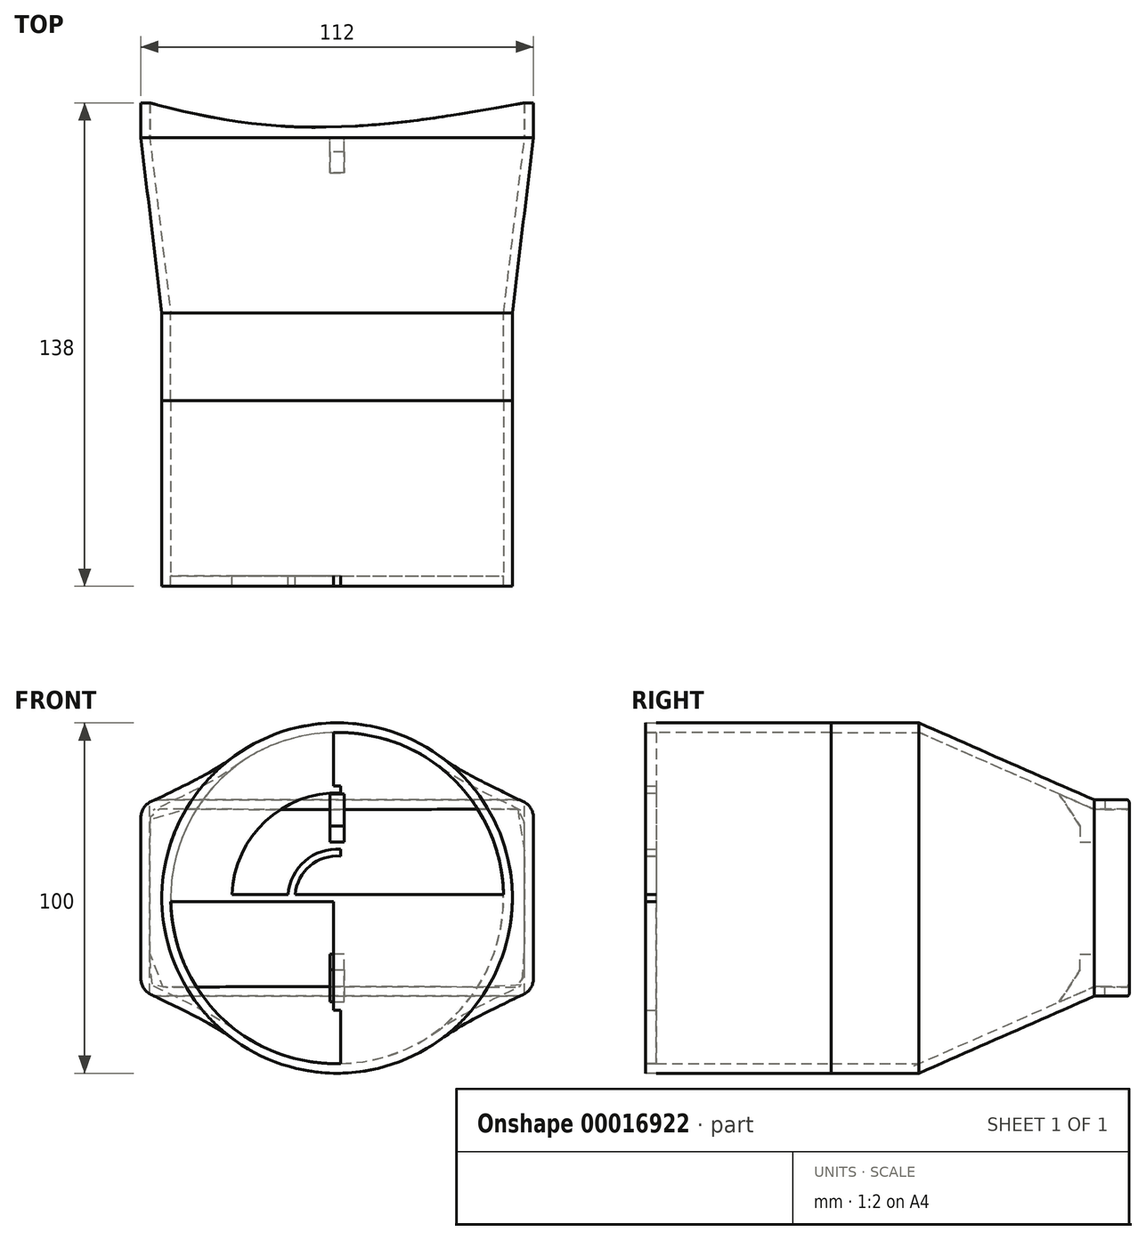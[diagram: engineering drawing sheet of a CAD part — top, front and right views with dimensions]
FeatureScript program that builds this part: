
annotation { "Feature Type Name" : "Feature", "Feature Type Description" : "" }
export const myFeature = defineFeature(function(context is Context, id is Id, definition is map)
    precondition{}
    {
        {
            var Q0;
            Q0=qCreatedBy(makeId("Front.planeOp"),FACE);
            var sketch = newSketch(context, id + "F0", { "sketchPlane" : qUnion([Q0])});
            skLineSegment(sketch, "E0.rect.bottom", {"start": v(51, 28) * mm, "end": v(-51, 28) * mm});
            skLineSegment(sketch, "E0.rect.top", {"start": v(51, -28) * mm, "end": v(-51, -28) * mm});
            skLineSegment(sketch, "E0.rect.left", {"start": v(56, 23) * mm, "end": v(56, -23) * mm});
            skLineSegment(sketch, "E0.rect.right", {"start": v(-56, 23) * mm, "end": v(-56, -23) * mm});
            skPoint(sketch, "E0.rect.middle", {"position": v(0, 0) * mm});
            skPoint(sketch, "E1.visualSharp", {"position": v(-56, 28) * mm});
            skArc(sketch, "E1.filletArc", {"start": v(-51, 28) * mm, "mid": v(-54.54, 26.54) * mm, "end": v(-56, 23) * mm});
            skPoint(sketch, "E2.visualSharp", {"position": v(-56, -28) * mm});
            skArc(sketch, "E2.filletArc", {"start": v(-56, -23) * mm, "mid": v(-54.54, -26.54) * mm, "end": v(-51, -28) * mm});
            skPoint(sketch, "E3.visualSharp", {"position": v(56, 28) * mm});
            skArc(sketch, "E3.filletArc", {"start": v(56, 23) * mm, "mid": v(54.54, 26.54) * mm, "end": v(51, 28) * mm});
            skPoint(sketch, "E4.visualSharp", {"position": v(56, -28) * mm});
            skArc(sketch, "E4.filletArc", {"start": v(51, -28) * mm, "mid": v(54.54, -26.54) * mm, "end": v(56, -23) * mm});
            skSolve(sketch);
        }
        {
            var Q0;
            Q0=qCreatedBy(makeId("Front.planeOp"),FACE);
            cPlane(context, id + "F1", {"entities" : qUnion([Q0]), "cplaneType" : CPlaneType.OFFSET, "offset" : 50 * mm, "width" : 150 * mm, "height" : 150 * mm});
        }
        {
            var Q0;
            Q0=qCreatedBy(id+"F1.planeOp",FACE);
            var sketch = newSketch(context, id + "F2", { "sketchPlane" : qUnion([Q0])});
            skPoint(sketch, "E5", {"position": v(-32.5, 38) * mm});
            skPoint(sketch, "E6", {"position": v(-39.41, 30.77) * mm});
            skPoint(sketch, "E7", {"position": v(-39.41, -30.77) * mm});
            skPoint(sketch, "E8", {"position": v(-32.5, -38) * mm});
            skPoint(sketch, "E9", {"position": v(32.5, -38) * mm});
            skPoint(sketch, "E10", {"position": v(39.41, -30.77) * mm});
            skPoint(sketch, "E11", {"position": v(39.41, 30.77) * mm});
            skPoint(sketch, "E12", {"position": v(32.5, 38) * mm});
            skArc(sketch, "E13", {"start": v(-32.63, 37.89) * mm, "mid": v(-36.24, 34.45) * mm, "end": v(-39.5, 30.66) * mm});
            skArc(sketch, "E14", {"start": v(-39.5, 30.66) * mm, "mid": v(-50, -0.08) * mm, "end": v(-39.4, -30.79) * mm});
            skArc(sketch, "E15", {"start": v(-39.4, -30.79) * mm, "mid": v(-36.12, -34.58) * mm, "end": v(-32.48, -38.02) * mm});
            skArc(sketch, "E16", {"start": v(-32.48, -38.02) * mm, "mid": v(0.03, -50) * mm, "end": v(32.52, -37.98) * mm});
            skArc(sketch, "E17", {"start": v(32.52, -37.98) * mm, "mid": v(36.14, -34.55) * mm, "end": v(39.4, -30.78) * mm});
            skArc(sketch, "E18", {"start": v(39.4, -30.78) * mm, "mid": v(50, -0.02) * mm, "end": v(39.42, 30.75) * mm});
            skArc(sketch, "E19", {"start": v(39.42, 30.75) * mm, "mid": v(36.13, 34.56) * mm, "end": v(32.48, 38.01) * mm});
            skArc(sketch, "E20", {"start": v(32.48, 38.01) * mm, "mid": v(-0.1, 50) * mm, "end": v(-32.63, 37.89) * mm});
            skSolve(sketch);
        }
        {
            var Q0;
            Q0 = qSketchRegion(id + "F0", true);
            var Q1;
            Q1 = qSketchRegion(id + "F2", true);
            loft(context, id + "F3", {"sheetProfilesArray" : [{ "sheetProfileEntities" : qUnion([Q0]) }, { "sheetProfileEntities" : qUnion([Q1]) }]});
        }
        {
            var Q0;
            Q0=makeQuery(id+"F3.opLoft","CAP_FACE",FACE,{"disambiguationData":[OSD([makeQuery(id+"F2.imprint","IMPRINT",FACE,{"disambiguationData":[TD([[makeQuery(id+"F2.imprint","IMPRINT",EDGE,{"derivedFrom":sQuery(id+"F2.wireOp",EDGE,"E13")}),1.0]])]})])],"isStart":true});
            var Q1;
            Q1=makeQuery(id+"F3.opLoft","CAP_FACE",FACE,{"disambiguationData":[OSD([makeQuery(id+"F0.imprint","IMPRINT",FACE,{"disambiguationData":[TD([[makeQuery(id+"F0.imprint","IMPRINT",EDGE,{"derivedFrom":sQuery(id+"F0.wireOp",EDGE,"E0.rect.bottom")}),1.0]])]})])],"isStart":true});
            var Q2;
            Q2=makeQuery(id+"F3.opLoft","SWEPT_BODY",BODY,{"disambiguationData":[OSD([makeQuery(id+"F0.imprint","IMPRINT",FACE,{"disambiguationData":[TD([[makeQuery(id+"F0.imprint","IMPRINT",EDGE,{"derivedFrom":sQuery(id+"F0.wireOp",EDGE,"E0.rect.bottom")}),1.0]])]}),makeQuery(id+"F2.imprint","IMPRINT",FACE,{"disambiguationData":[TD([[makeQuery(id+"F2.imprint","IMPRINT",EDGE,{"derivedFrom":sQuery(id+"F2.wireOp",EDGE,"20035c58-e152-4f65-9b51-79b2b6d4c0861")}),1.0]])]})])]});
            shell(context, id + "F4", {"entities" : qUnion([Q0, Q1]), "parts" : qUnion([Q2]), "thickness" : 2.5 * mm});
        }
        {
            var Q0;
            Q0=makeQuery(id+"F3.opLoft","CAP_FACE",FACE,{"disambiguationData":[OSD([makeQuery(id+"F2.imprint","IMPRINT",FACE,{"disambiguationData":[TD([[makeQuery(id+"F2.imprint","IMPRINT",EDGE,{"derivedFrom":sQuery(id+"F2.wireOp",EDGE,"E13")}),1.0]])]})])],"isStart":true});
            extrude(context, id + "F5", {"entities" : qUnion([Q0]), "operationType" : NewBodyOperationType.ADD, "depth" : 25 * mm});
        }
        {
            var Q0;
            Q0=makeQuery(id+"F3.opLoft","CAP_FACE",FACE,{"disambiguationData":[OSD([makeQuery(id+"F0.imprint","IMPRINT",FACE,{"disambiguationData":[TD([[makeQuery(id+"F0.imprint","IMPRINT",EDGE,{"derivedFrom":sQuery(id+"F0.wireOp",EDGE,"E0.rect.bottom")}),1.0]])]})])],"isStart":true});
            extrude(context, id + "F6", {"entities" : qUnion([Q0]), "operationType" : NewBodyOperationType.ADD, "depth" : 10 * mm});
        }
        {
            var Q0;
            Q0=makeQuery(id+"F6.opExtrude","SWEPT_FACE",FACE,{"disambiguationData":[OSD([sQuery(id+"F0.wireOp",EDGE,"E0.rect.bottom"),sQuery(id+"F0.wireOp",EDGE,"E1.filletArc"),sQuery(id+"F0.wireOp",EDGE,"E3.filletArc")])]});
            var sketch = newSketch(context, id + "F7", { "sketchPlane" : qUnion([Q0])});
            skPoint(sketch, "E21.0", {"position": v(-56, 10) * mm});
            skPoint(sketch, "E22.0", {"position": v(56, 10) * mm});
            skFitSpline(sketch, "E23", {"points": [v(-53.5, 10) * mm, v(-11.54, 3.12) * mm, v(53.5, 10) * mm], "startDerivative": vector(83.97, -22.89) * mm, "endDerivative": vector(135.93, 25.6) * mm});
            skLineSegment(sketch, "E24", {"start": v(-53.5, 10) * mm, "end": v(53.5, 10) * mm});
            skSolve(sketch);
        }
        {
            var Q0;
            Q0 = qSketchRegion(id + "F7", true);
            extrude(context, id + "F8", {"entities" : qUnion([Q0]), "operationType" : NewBodyOperationType.REMOVE, "endBound" : BoundingType.THROUGH_ALL, "oppositeDirection" : true, "depth" : 25 * mm});
        }
        {
            var Q0;
            Q0=makeQuery(id+"F5.opExtrude","CAP_FACE",FACE,{"disambiguationData":[OSD([makeQuery(id+"F2.imprint","IMPRINT",FACE,{"disambiguationData":[TD([[makeQuery(id+"F2.imprint","IMPRINT",EDGE,{"derivedFrom":sQuery(id+"F2.wireOp",EDGE,"E13")}),1.0]])]})])],"isStart":false});
            extrude(context, id + "F9", {"entities" : qUnion([Q0]), "depth" : 50 * mm});
        }
        {
            var Q0;
            Q0=makeQuery(id+"F9.opExtrude","CAP_FACE",FACE,{"disambiguationData":[OSD([makeQuery(id+"F2.imprint","IMPRINT",FACE,{"disambiguationData":[TD([[makeQuery(id+"F2.imprint","IMPRINT",EDGE,{"derivedFrom":sQuery(id+"F2.wireOp",EDGE,"E13")}),1.0]])]})])],"isStart":false});
            var sketch = newSketch(context, id + "F10", { "sketchPlane" : qUnion([Q0])});
            skCircle(sketch, "E25", {"center": v(0, 0) * mm, "radius": 50 * mm});
            skCircle(sketch, "E26", {"center": v(0, 0) * mm, "radius": 32 * mm});
            skCircle(sketch, "E27", {"center": v(0, 0) * mm, "radius": 30 * mm});
            skCircle(sketch, "E28", {"center": v(0, 0) * mm, "radius": 14 * mm});
            skCircle(sketch, "E29", {"center": v(0, 0) * mm, "radius": 12 * mm});
            skLineSegment(sketch, "E30.rect.bottom", {"start": v(1, 50) * mm, "end": v(-1, 50) * mm});
            skLineSegment(sketch, "E30.rect.top", {"start": v(1, -50) * mm, "end": v(-1, -50) * mm});
            skLineSegment(sketch, "E30.rect.left", {"start": v(1, 50) * mm, "end": v(1, -50) * mm});
            skLineSegment(sketch, "E30.rect.right", {"start": v(-1, 50) * mm, "end": v(-1, -50) * mm});
            skLineSegment(sketch, "E31.rect.bottom", {"start": v(-50, 1) * mm, "end": v(50, 1) * mm});
            skLineSegment(sketch, "E31.rect.top", {"start": v(-50, -1) * mm, "end": v(50, -1) * mm});
            skLineSegment(sketch, "E31.rect.left", {"start": v(-50, 1) * mm, "end": v(-50, -1) * mm});
            skLineSegment(sketch, "E31.rect.right", {"start": v(50, 1) * mm, "end": v(50, -1) * mm});
            skSolve(sketch);
        }
        {
            var Q0;
            {var subQ5=sQuery(id+"F10.wireOp",EDGE,"E25");var subQ7=makeQuery(id+"F10.imprint","IMPRINT",VERTEX,{"disambiguationData":[OD(0.0)],"derivedFrom":subQ5});Q0=makeQuery(id+"F10.imprint","IMPRINT",FACE,{"disambiguationData":[TD([[makeQuery(id+"F10.imprint","IMPRINT",EDGE,{"disambiguationData":[TD([[subQ7,-1.0]])],"derivedFrom":subQ5}),1.0]])]});}
            var Q1;
            {var subQ6=sQuery(id+"F10.wireOp",EDGE,"E30.rect.bottom");Q1=makeQuery(id+"F10.imprint","IMPRINT",FACE,{"disambiguationData":[TD([[makeQuery(id+"F10.imprint","IMPRINT",EDGE,{"derivedFrom":subQ6}),1.0]])]});}
            var Q2;
            {var subQ3=sQuery(id+"F10.wireOp",EDGE,"E25");var subQ8=makeQuery(id+"F10.imprint","IMPRINT",VERTEX,{"disambiguationData":[OD(6.0)],"derivedFrom":subQ3});Q2=makeQuery(id+"F10.imprint","IMPRINT",FACE,{"disambiguationData":[TD([[makeQuery(id+"F10.imprint","IMPRINT",EDGE,{"disambiguationData":[TD([[subQ8,-1.0]])],"derivedFrom":subQ3}),1.0]])]});}
            var Q3;
            {var subQ5=sQuery(id+"F10.wireOp",EDGE,"E31.rect.right");Q3=makeQuery(id+"F10.imprint","IMPRINT",FACE,{"disambiguationData":[TD([[makeQuery(id+"F10.imprint","IMPRINT",EDGE,{"derivedFrom":subQ5}),-1.0]])]});}
            var Q4;
            {var subQ5=sQuery(id+"F10.wireOp",EDGE,"E25");var subQ8=makeQuery(id+"F10.imprint","IMPRINT",VERTEX,{"disambiguationData":[OD(4.0)],"derivedFrom":subQ5});Q4=makeQuery(id+"F10.imprint","IMPRINT",FACE,{"disambiguationData":[TD([[makeQuery(id+"F10.imprint","IMPRINT",EDGE,{"disambiguationData":[TD([[subQ8,-1.0]])],"derivedFrom":subQ5}),1.0]])]});}
            var Q5;
            {var subQ6=sQuery(id+"F10.wireOp",EDGE,"E30.rect.top");Q5=makeQuery(id+"F10.imprint","IMPRINT",FACE,{"disambiguationData":[TD([[makeQuery(id+"F10.imprint","IMPRINT",EDGE,{"derivedFrom":subQ6}),-1.0]])]});}
            var Q6;
            {var subQ5=sQuery(id+"F10.wireOp",EDGE,"E25");var subQ8=makeQuery(id+"F10.imprint","IMPRINT",VERTEX,{"disambiguationData":[OD(2.0)],"derivedFrom":subQ5});Q6=makeQuery(id+"F10.imprint","IMPRINT",FACE,{"disambiguationData":[TD([[makeQuery(id+"F10.imprint","IMPRINT",EDGE,{"disambiguationData":[TD([[subQ8,-1.0]])],"derivedFrom":subQ5}),1.0]])]});}
            var Q7;
            {var subQ0=sQuery(id+"F10.wireOp",EDGE,"E31.rect.left");Q7=makeQuery(id+"F10.imprint","IMPRINT",FACE,{"disambiguationData":[TD([[makeQuery(id+"F10.imprint","IMPRINT",EDGE,{"derivedFrom":subQ0}),1.0]])]});}
            var Q8;
            {var subQ3=sQuery(id+"F10.wireOp",EDGE,"E31.rect.bottom");var subQ5=sQuery(id+"F10.wireOp",EDGE,"E26");var subQ7=makeQuery(id+"F10.imprint","INTERSECT",VERTEX,{"disambiguationData":[OD(1.0)],"derivedFrom":[subQ5,subQ3]});Q8=makeQuery(id+"F10.imprint","IMPRINT",FACE,{"disambiguationData":[TD([[makeQuery(id+"F10.imprint","IMPRINT",EDGE,{"disambiguationData":[TD([[subQ7,-1.0]])],"derivedFrom":subQ5}),-1.0]])]});}
            var Q9;
            {var subQ3=sQuery(id+"F10.wireOp",EDGE,"E26");var subQ5=sQuery(id+"F10.wireOp",EDGE,"E31.rect.bottom");var subQ7=makeQuery(id+"F10.imprint","INTERSECT",VERTEX,{"disambiguationData":[OD(1.0)],"derivedFrom":[subQ3,subQ5]});Q9=makeQuery(id+"F10.imprint","IMPRINT",FACE,{"disambiguationData":[TD([[makeQuery(id+"F10.imprint","IMPRINT",EDGE,{"disambiguationData":[TD([[subQ7,-1.0]])],"derivedFrom":subQ3}),1.0]])]});}
            var Q10;
            {var subQ3=sQuery(id+"F10.wireOp",EDGE,"E27");var subQ5=sQuery(id+"F10.wireOp",EDGE,"E31.rect.bottom");var subQ7=makeQuery(id+"F10.imprint","INTERSECT",VERTEX,{"disambiguationData":[OD(1.0)],"derivedFrom":[subQ3,subQ5]});Q10=makeQuery(id+"F10.imprint","IMPRINT",FACE,{"disambiguationData":[TD([[makeQuery(id+"F10.imprint","IMPRINT",EDGE,{"disambiguationData":[TD([[subQ7,-1.0]])],"derivedFrom":subQ3}),1.0]])]});}
            var Q11;
            {var subQ3=sQuery(id+"F10.wireOp",EDGE,"E26");var subQ5=sQuery(id+"F10.wireOp",EDGE,"E30.rect.right");var subQ7=makeQuery(id+"F10.imprint","INTERSECT",VERTEX,{"disambiguationData":[OD(0.0)],"derivedFrom":[subQ3,subQ5]});Q11=makeQuery(id+"F10.imprint","IMPRINT",FACE,{"disambiguationData":[TD([[makeQuery(id+"F10.imprint","IMPRINT",EDGE,{"disambiguationData":[TD([[subQ7,-1.0]])],"derivedFrom":subQ3}),1.0]])]});}
            var Q12;
            {var subQ0=sQuery(id+"F10.wireOp",EDGE,"E31.rect.top");var subQ3=sQuery(id+"F10.wireOp",EDGE,"E26");var subQ4=makeQuery(id+"F10.imprint","INTERSECT",VERTEX,{"disambiguationData":[OD(0.0)],"derivedFrom":[subQ3,subQ0]});Q12=makeQuery(id+"F10.imprint","IMPRINT",FACE,{"disambiguationData":[TD([[makeQuery(id+"F10.imprint","IMPRINT",EDGE,{"disambiguationData":[TD([[subQ4,-1.0]])],"derivedFrom":subQ3}),1.0]])]});}
            var Q13;
            {var subQ0=sQuery(id+"F10.wireOp",EDGE,"E31.rect.top");var subQ3=sQuery(id+"F10.wireOp",EDGE,"E28");var subQ4=makeQuery(id+"F10.imprint","INTERSECT",VERTEX,{"disambiguationData":[OD(0.0)],"derivedFrom":[subQ3,subQ0]});Q13=makeQuery(id+"F10.imprint","IMPRINT",FACE,{"disambiguationData":[TD([[makeQuery(id+"F10.imprint","IMPRINT",EDGE,{"disambiguationData":[TD([[subQ4,-1.0]])],"derivedFrom":subQ3}),1.0]])]});}
            var Q14;
            {var subQ3=sQuery(id+"F10.wireOp",EDGE,"E28");var subQ5=sQuery(id+"F10.wireOp",EDGE,"E30.rect.right");var subQ7=makeQuery(id+"F10.imprint","INTERSECT",VERTEX,{"disambiguationData":[OD(0.0)],"derivedFrom":[subQ3,subQ5]});Q14=makeQuery(id+"F10.imprint","IMPRINT",FACE,{"disambiguationData":[TD([[makeQuery(id+"F10.imprint","IMPRINT",EDGE,{"disambiguationData":[TD([[subQ7,-1.0]])],"derivedFrom":subQ3}),1.0]])]});}
            var Q15;
            {var subQ3=sQuery(id+"F10.wireOp",EDGE,"E28");var subQ5=sQuery(id+"F10.wireOp",EDGE,"E31.rect.bottom");var subQ7=makeQuery(id+"F10.imprint","INTERSECT",VERTEX,{"disambiguationData":[OD(1.0)],"derivedFrom":[subQ3,subQ5]});Q15=makeQuery(id+"F10.imprint","IMPRINT",FACE,{"disambiguationData":[TD([[makeQuery(id+"F10.imprint","IMPRINT",EDGE,{"disambiguationData":[TD([[subQ7,-1.0]])],"derivedFrom":subQ3}),1.0]])]});}
            var Q16;
            {var subQ3=sQuery(id+"F10.wireOp",EDGE,"E29");var subQ5=sQuery(id+"F10.wireOp",EDGE,"E31.rect.bottom");var subQ7=makeQuery(id+"F10.imprint","INTERSECT",VERTEX,{"disambiguationData":[OD(1.0)],"derivedFrom":[subQ3,subQ5]});Q16=makeQuery(id+"F10.imprint","IMPRINT",FACE,{"disambiguationData":[TD([[makeQuery(id+"F10.imprint","IMPRINT",EDGE,{"disambiguationData":[TD([[subQ7,-1.0]])],"derivedFrom":subQ3}),1.0]])]});}
            var Q17;
            {var subQ3=sQuery(id+"F10.wireOp",EDGE,"E30.rect.left");var subQ5=sQuery(id+"F10.wireOp",EDGE,"E29");var subQ7=makeQuery(id+"F10.imprint","INTERSECT",VERTEX,{"disambiguationData":[OD(0.0)],"derivedFrom":[subQ5,subQ3]});Q17=makeQuery(id+"F10.imprint","IMPRINT",FACE,{"disambiguationData":[TD([[makeQuery(id+"F10.imprint","IMPRINT",EDGE,{"disambiguationData":[TD([[subQ7,-1.0]])],"derivedFrom":subQ5}),1.0]])]});}
            var Q18;
            {var subQ1=sQuery(id+"F10.wireOp",EDGE,"E30.rect.right");var subQ5=sQuery(id+"F10.wireOp",EDGE,"E29");var subQ6=makeQuery(id+"F10.imprint","INTERSECT",VERTEX,{"disambiguationData":[OD(1.0)],"derivedFrom":[subQ5,subQ1]});Q18=makeQuery(id+"F10.imprint","IMPRINT",FACE,{"disambiguationData":[TD([[makeQuery(id+"F10.imprint","IMPRINT",EDGE,{"disambiguationData":[TD([[subQ6,-1.0]])],"derivedFrom":subQ5}),1.0]])]});}
            var Q19;
            {var subQ3=sQuery(id+"F10.wireOp",EDGE,"E29");var subQ5=sQuery(id+"F10.wireOp",EDGE,"E31.rect.bottom");var subQ7=makeQuery(id+"F10.imprint","INTERSECT",VERTEX,{"disambiguationData":[OD(0.0)],"derivedFrom":[subQ3,subQ5]});Q19=makeQuery(id+"F10.imprint","IMPRINT",FACE,{"disambiguationData":[TD([[makeQuery(id+"F10.imprint","IMPRINT",EDGE,{"disambiguationData":[TD([[subQ7,1.0]])],"derivedFrom":subQ3}),1.0]])]});}
            var Q20;
            {var subQ3=sQuery(id+"F10.wireOp",EDGE,"E28");var subQ5=sQuery(id+"F10.wireOp",EDGE,"E30.rect.left");var subQ7=makeQuery(id+"F10.imprint","INTERSECT",VERTEX,{"disambiguationData":[OD(1.0)],"derivedFrom":[subQ3,subQ5]});Q20=makeQuery(id+"F10.imprint","IMPRINT",FACE,{"disambiguationData":[TD([[makeQuery(id+"F10.imprint","IMPRINT",EDGE,{"disambiguationData":[TD([[subQ7,-1.0]])],"derivedFrom":subQ3}),1.0]])]});}
            var Q21;
            {var subQ0=sQuery(id+"F10.wireOp",EDGE,"E30.rect.right");var subQ3=sQuery(id+"F10.wireOp",EDGE,"E28");var subQ4=makeQuery(id+"F10.imprint","INTERSECT",VERTEX,{"disambiguationData":[OD(1.0)],"derivedFrom":[subQ3,subQ0]});Q21=makeQuery(id+"F10.imprint","IMPRINT",FACE,{"disambiguationData":[TD([[makeQuery(id+"F10.imprint","IMPRINT",EDGE,{"disambiguationData":[TD([[subQ4,-1.0]])],"derivedFrom":subQ3}),1.0]])]});}
            var Q22;
            {var subQ0=sQuery(id+"F10.wireOp",EDGE,"E30.rect.right");var subQ3=sQuery(id+"F10.wireOp",EDGE,"E27");var subQ4=makeQuery(id+"F10.imprint","INTERSECT",VERTEX,{"disambiguationData":[OD(1.0)],"derivedFrom":[subQ3,subQ0]});Q22=makeQuery(id+"F10.imprint","IMPRINT",FACE,{"disambiguationData":[TD([[makeQuery(id+"F10.imprint","IMPRINT",EDGE,{"disambiguationData":[TD([[subQ4,-1.0]])],"derivedFrom":subQ3}),1.0]])]});}
            var Q23;
            {var subQ3=sQuery(id+"F10.wireOp",EDGE,"E28");var subQ5=sQuery(id+"F10.wireOp",EDGE,"E31.rect.bottom");var subQ7=makeQuery(id+"F10.imprint","INTERSECT",VERTEX,{"disambiguationData":[OD(0.0)],"derivedFrom":[subQ3,subQ5]});Q23=makeQuery(id+"F10.imprint","IMPRINT",FACE,{"disambiguationData":[TD([[makeQuery(id+"F10.imprint","IMPRINT",EDGE,{"disambiguationData":[TD([[subQ7,1.0]])],"derivedFrom":subQ3}),1.0]])]});}
            var Q24;
            {var subQ3=sQuery(id+"F10.wireOp",EDGE,"E28");var subQ5=sQuery(id+"F10.wireOp",EDGE,"E30.rect.left");var subQ7=makeQuery(id+"F10.imprint","INTERSECT",VERTEX,{"disambiguationData":[OD(0.0)],"derivedFrom":[subQ3,subQ5]});Q24=makeQuery(id+"F10.imprint","IMPRINT",FACE,{"disambiguationData":[TD([[makeQuery(id+"F10.imprint","IMPRINT",EDGE,{"disambiguationData":[TD([[subQ7,1.0]])],"derivedFrom":subQ3}),1.0]])]});}
            var Q25;
            {var subQ3=sQuery(id+"F10.wireOp",EDGE,"E28");var subQ5=sQuery(id+"F10.wireOp",EDGE,"E30.rect.left");var subQ7=makeQuery(id+"F10.imprint","INTERSECT",VERTEX,{"disambiguationData":[OD(0.0)],"derivedFrom":[subQ3,subQ5]});Q25=makeQuery(id+"F10.imprint","IMPRINT",FACE,{"disambiguationData":[TD([[makeQuery(id+"F10.imprint","IMPRINT",EDGE,{"disambiguationData":[TD([[subQ7,-1.0]])],"derivedFrom":subQ3}),1.0]])]});}
            var Q26;
            {var subQ3=sQuery(id+"F10.wireOp",EDGE,"E27");var subQ5=sQuery(id+"F10.wireOp",EDGE,"E30.rect.left");var subQ7=makeQuery(id+"F10.imprint","INTERSECT",VERTEX,{"disambiguationData":[OD(0.0)],"derivedFrom":[subQ3,subQ5]});Q26=makeQuery(id+"F10.imprint","IMPRINT",FACE,{"disambiguationData":[TD([[makeQuery(id+"F10.imprint","IMPRINT",EDGE,{"disambiguationData":[TD([[subQ7,-1.0]])],"derivedFrom":subQ3}),1.0]])]});}
            var Q27;
            {var subQ3=sQuery(id+"F10.wireOp",EDGE,"E30.rect.left");var subQ5=sQuery(id+"F10.wireOp",EDGE,"E26");var subQ6=makeQuery(id+"F10.imprint","INTERSECT",VERTEX,{"disambiguationData":[OD(0.0)],"derivedFrom":[subQ5,subQ3]});Q27=makeQuery(id+"F10.imprint","IMPRINT",FACE,{"disambiguationData":[TD([[makeQuery(id+"F10.imprint","IMPRINT",EDGE,{"disambiguationData":[TD([[subQ6,-1.0]])],"derivedFrom":subQ5}),-1.0]])]});}
            var Q28;
            {var subQ3=sQuery(id+"F10.wireOp",EDGE,"E26");var subQ5=sQuery(id+"F10.wireOp",EDGE,"E30.rect.left");var subQ7=makeQuery(id+"F10.imprint","INTERSECT",VERTEX,{"disambiguationData":[OD(0.0)],"derivedFrom":[subQ3,subQ5]});Q28=makeQuery(id+"F10.imprint","IMPRINT",FACE,{"disambiguationData":[TD([[makeQuery(id+"F10.imprint","IMPRINT",EDGE,{"disambiguationData":[TD([[subQ7,-1.0]])],"derivedFrom":subQ3}),1.0]])]});}
            var Q29;
            {var subQ3=sQuery(id+"F10.wireOp",EDGE,"E26");var subQ5=sQuery(id+"F10.wireOp",EDGE,"E30.rect.left");var subQ7=makeQuery(id+"F10.imprint","INTERSECT",VERTEX,{"disambiguationData":[OD(0.0)],"derivedFrom":[subQ3,subQ5]});Q29=makeQuery(id+"F10.imprint","IMPRINT",FACE,{"disambiguationData":[TD([[makeQuery(id+"F10.imprint","IMPRINT",EDGE,{"disambiguationData":[TD([[subQ7,1.0]])],"derivedFrom":subQ3}),1.0]])]});}
            var Q30;
            {var subQ3=sQuery(id+"F10.wireOp",EDGE,"E31.rect.bottom");var subQ5=sQuery(id+"F10.wireOp",EDGE,"E26");var subQ7=makeQuery(id+"F10.imprint","INTERSECT",VERTEX,{"disambiguationData":[OD(0.0)],"derivedFrom":[subQ5,subQ3]});Q30=makeQuery(id+"F10.imprint","IMPRINT",FACE,{"disambiguationData":[TD([[makeQuery(id+"F10.imprint","IMPRINT",EDGE,{"disambiguationData":[TD([[subQ7,1.0]])],"derivedFrom":subQ5}),-1.0]])]});}
            var Q31;
            {var subQ3=sQuery(id+"F10.wireOp",EDGE,"E26");var subQ5=sQuery(id+"F10.wireOp",EDGE,"E30.rect.left");var subQ7=makeQuery(id+"F10.imprint","INTERSECT",VERTEX,{"disambiguationData":[OD(1.0)],"derivedFrom":[subQ3,subQ5]});Q31=makeQuery(id+"F10.imprint","IMPRINT",FACE,{"disambiguationData":[TD([[makeQuery(id+"F10.imprint","IMPRINT",EDGE,{"disambiguationData":[TD([[subQ7,-1.0]])],"derivedFrom":subQ3}),1.0]])]});}
            var Q32;
            {var subQ3=sQuery(id+"F10.wireOp",EDGE,"E26");var subQ5=sQuery(id+"F10.wireOp",EDGE,"E31.rect.bottom");var subQ7=makeQuery(id+"F10.imprint","INTERSECT",VERTEX,{"disambiguationData":[OD(0.0)],"derivedFrom":[subQ3,subQ5]});Q32=makeQuery(id+"F10.imprint","IMPRINT",FACE,{"disambiguationData":[TD([[makeQuery(id+"F10.imprint","IMPRINT",EDGE,{"disambiguationData":[TD([[subQ7,1.0]])],"derivedFrom":subQ3}),1.0]])]});}
            var Q33;
            {var subQ0=sQuery(id+"F10.wireOp",EDGE,"E31.rect.bottom");var subQ3=sQuery(id+"F10.wireOp",EDGE,"E30.rect.left");var subQ4=makeQuery(id+"F10.imprint","INTERSECT",VERTEX,{"derivedFrom":[subQ3,subQ0]});Q33=makeQuery(id+"F10.imprint","IMPRINT",FACE,{"disambiguationData":[TD([[makeQuery(id+"F10.imprint","IMPRINT",EDGE,{"disambiguationData":[TD([[subQ4,-1.0]])],"derivedFrom":subQ3}),-1.0]])]});}
            var Q34;
            {var subQ3=sQuery(id+"F10.wireOp",EDGE,"E27");var subQ5=sQuery(id+"F10.wireOp",EDGE,"E31.rect.bottom");var subQ7=makeQuery(id+"F10.imprint","INTERSECT",VERTEX,{"disambiguationData":[OD(0.0)],"derivedFrom":[subQ3,subQ5]});Q34=makeQuery(id+"F10.imprint","IMPRINT",FACE,{"disambiguationData":[TD([[makeQuery(id+"F10.imprint","IMPRINT",EDGE,{"disambiguationData":[TD([[subQ7,1.0]])],"derivedFrom":subQ3}),1.0]])]});}
            var Q35;
            {var subQ3=sQuery(id+"F10.wireOp",EDGE,"E26");var subQ5=sQuery(id+"F10.wireOp",EDGE,"E30.rect.right");var subQ7=makeQuery(id+"F10.imprint","INTERSECT",VERTEX,{"disambiguationData":[OD(1.0)],"derivedFrom":[subQ3,subQ5]});Q35=makeQuery(id+"F10.imprint","IMPRINT",FACE,{"disambiguationData":[TD([[makeQuery(id+"F10.imprint","IMPRINT",EDGE,{"disambiguationData":[TD([[subQ7,-1.0]])],"derivedFrom":subQ3}),1.0]])]});}
            var Q36;
            {var subQ1=sQuery(id+"F10.wireOp",EDGE,"E30.rect.right");var subQ5=sQuery(id+"F10.wireOp",EDGE,"E26");var subQ6=makeQuery(id+"F10.imprint","INTERSECT",VERTEX,{"disambiguationData":[OD(1.0)],"derivedFrom":[subQ5,subQ1]});Q36=makeQuery(id+"F10.imprint","IMPRINT",FACE,{"disambiguationData":[TD([[makeQuery(id+"F10.imprint","IMPRINT",EDGE,{"disambiguationData":[TD([[subQ6,-1.0]])],"derivedFrom":subQ5}),-1.0]])]});}
            extrude(context, id + "F11", {"entities" : qUnion([Q0, Q1, Q2, Q3, Q4, Q5, Q6, Q7, Q8, Q9, Q10, Q11, Q12, Q13, Q14, Q15, Q16, Q17, Q18, Q19, Q20, Q21, Q22, Q23, Q24, Q25, Q26, Q27, Q28, Q29, Q30, Q31, Q32, Q33, Q34, Q35, Q36]), "operationType" : NewBodyOperationType.ADD, "depth" : 3 * mm});
        }
        {
            var Q0;
            Q0=qCreatedBy(makeId("Front.planeOp"),FACE);
            var sketch = newSketch(context, id + "F12", { "sketchPlane" : qUnion([Q0])});
            skFitSpline(sketch, "E32.0", {"points": [v(53.38, 22.27) * mm, v(53.41, 19.48) * mm, v(53.44, 16.3) * mm, v(53.46, 12.9) * mm, v(53.46, 12.73) * mm, v(53.47, 10.09) * mm, v(53.48, 6.93) * mm, v(53.48, 3.38) * mm, v(53.48, 3.2) * mm, v(53.49, -4.03) * mm, v(53.47, -10.46) * mm, v(53.44, -15.63) * mm, v(53.44, -15.9) * mm, v(53.43, -17.43) * mm, v(53.41, -19.03) * mm, v(53.4, -20.57) * mm, v(53.4, -20.66) * mm, v(53.38, -21.6) * mm, v(53.38, -22.4) * mm, v(53.37, -23.01) * mm, v(53.37, -23.05) * mm, v(53.37, -23.15) * mm, v(53.36, -23.25) * mm, v(53.35, -23.34) * mm, v(53.35, -23.34) * mm, v(53.34, -23.44) * mm, v(53.32, -23.54) * mm, v(53.3, -23.63) * mm, v(53.3, -23.64) * mm, v(53.26, -23.83) * mm, v(53.2, -24.01) * mm, v(53.11, -24.2) * mm, v(53.1, -24.2) * mm, v(53.02, -24.37) * mm, v(52.92, -24.54) * mm, v(52.8, -24.7) * mm, v(52.78, -24.7) * mm, v(52.66, -24.85) * mm, v(52.52, -24.98) * mm, v(52.36, -25.1) * mm, v(52.35, -25.1) * mm, v(52.17, -25.22) * mm, v(51.97, -25.32) * mm, v(51.75, -25.38) * mm, v(51.74, -25.38) * mm, v(51.66, -25.4) * mm, v(51.58, -25.42) * mm, v(51.5, -25.43) * mm, v(51.5, -25.43) * mm, v(51.42, -25.44) * mm, v(51.34, -25.45) * mm, v(51.25, -25.45) * mm, v(51.24, -25.45) * mm, v(51.22, -25.45) * mm, v(50.84, -25.45) * mm, v(50.1, -25.44) * mm, v(50.06, -25.44) * mm, v(49.53, -25.44) * mm, v(48.76, -25.44) * mm, v(47.74, -25.43) * mm, v(47.7, -25.43) * mm, v(45.66, -25.42) * mm, v(44.06, -25.4) * mm, v(43, -25.4) * mm, v(42.95, -25.4) * mm, v(36.58, -25.36) * mm, v(30.22, -25.33) * mm, v(24.24, -25.31) * mm, v(23.94, -25.3) * mm, v(11.9, -25.27) * mm, v(-0.86, -25.26) * mm, v(-13.71, -25.28) * mm, v(-14.37, -25.28) * mm, v(-20.37, -25.3) * mm, v(-26.76, -25.32) * mm, v(-33.18, -25.35) * mm, v(-33.53, -25.35) * mm, v(-36.23, -25.36) * mm, v(-39.37, -25.38) * mm, v(-42.8, -25.4) * mm, v(-43, -25.4) * mm, v(-44.17, -25.4) * mm, v(-45.72, -25.42) * mm, v(-47.6, -25.43) * mm, v(-47.7, -25.43) * mm, v(-48.79, -25.44) * mm, v(-49.59, -25.44) * mm, v(-50.02, -25.44) * mm, v(-50.04, -25.44) * mm, v(-50.76, -25.45) * mm, v(-51.17, -25.45) * mm, v(-51.21, -25.45) * mm, v(-51.21, -25.45) * mm, v(-51.27, -25.45) * mm, v(-51.33, -25.45) * mm, v(-51.38, -25.44) * mm, v(-51.38, -25.44) * mm, v(-51.43, -25.44) * mm, v(-51.49, -25.43) * mm, v(-51.54, -25.42) * mm, v(-51.55, -25.42) * mm, v(-51.65, -25.4) * mm, v(-51.76, -25.38) * mm, v(-51.87, -25.34) * mm, v(-51.87, -25.34) * mm, v(-52.02, -25.29) * mm, v(-52.17, -25.21) * mm, v(-52.32, -25.12) * mm, v(-52.32, -25.12) * mm, v(-52.48, -25.01) * mm, v(-52.62, -24.88) * mm, v(-52.76, -24.73) * mm, v(-52.77, -24.72) * mm, v(-52.89, -24.58) * mm, v(-53, -24.42) * mm, v(-53.09, -24.23) * mm, v(-53.1, -24.22) * mm, v(-53.18, -24.05) * mm, v(-53.25, -23.87) * mm, v(-53.3, -23.67) * mm, v(-53.3, -23.66) * mm, v(-53.32, -23.57) * mm, v(-53.34, -23.47) * mm, v(-53.35, -23.37) * mm, v(-53.35, -23.36) * mm, v(-53.36, -23.27) * mm, v(-53.36, -23.17) * mm, v(-53.37, -23.06) * mm, v(-53.37, -23.06) * mm, v(-53.38, -22.3) * mm, v(-53.39, -21.48) * mm, v(-53.4, -20.66) * mm, v(-53.4, -20.62) * mm, v(-53.41, -19.13) * mm, v(-53.43, -17.51) * mm, v(-53.44, -15.83) * mm, v(-53.44, -15.74) * mm, v(-53.46, -13) * mm, v(-53.47, -9.76) * mm, v(-53.48, -6.18) * mm, v(-53.48, -6) * mm, v(-53.48, -2.98) * mm, v(-53.48, 0.27) * mm, v(-53.48, 3.58) * mm, v(-53.48, 3.76) * mm, v(-53.48, 7.15) * mm, v(-53.47, 10.41) * mm, v(-53.45, 13.35) * mm, v(-53.45, 13.5) * mm, v(-53.44, 15.11) * mm, v(-53.43, 16.74) * mm, v(-53.42, 18.3) * mm, v(-53.42, 18.38) * mm, v(-53.41, 19.16) * mm, v(-53.4, 19.97) * mm, v(-53.4, 20.77) * mm, v(-53.4, 20.82) * mm, v(-53.4, 21.13) * mm, v(-53.39, 21.45) * mm, v(-53.38, 21.78) * mm, v(-53.38, 21.8) * mm, v(-53.38, 21.98) * mm, v(-53.38, 22.17) * mm, v(-53.38, 22.37) * mm, v(-53.38, 22.38) * mm, v(-53.37, 22.52) * mm, v(-53.37, 22.66) * mm, v(-53.37, 22.81) * mm, v(-53.37, 22.82) * mm, v(-53.37, 22.94) * mm, v(-53.37, 23.02) * mm, v(-53.37, 23.04) * mm, v(-53.37, 23.04) * mm, v(-53.37, 23.12) * mm, v(-53.36, 23.2) * mm, v(-53.36, 23.25) * mm, v(-53.36, 23.26) * mm, v(-53.35, 23.45) * mm, v(-53.3, 23.65) * mm, v(-53.25, 23.85) * mm, v(-53.24, 23.86) * mm, v(-53.18, 24.05) * mm, v(-53.1, 24.24) * mm, v(-52.99, 24.42) * mm, v(-52.98, 24.43) * mm, v(-52.87, 24.6) * mm, v(-52.74, 24.76) * mm, v(-52.6, 24.9) * mm, v(-52.58, 24.91) * mm, v(-52.44, 25.05) * mm, v(-52.27, 25.16) * mm, v(-52.08, 25.25) * mm, v(-52.07, 25.26) * mm, v(-51.9, 25.34) * mm, v(-51.7, 25.4) * mm, v(-51.5, 25.43) * mm, v(-51.49, 25.43) * mm, v(-51.44, 25.44) * mm, v(-51.39, 25.44) * mm, v(-51.34, 25.45) * mm, v(-51.33, 25.45) * mm, v(-51.3, 25.45) * mm, v(-51.24, 25.45) * mm, v(-51.18, 25.45) * mm, v(-51.18, 25.45) * mm, v(-51.15, 25.45) * mm, v(-51.1, 25.45) * mm, v(-51.03, 25.45) * mm, v(-51.03, 25.45) * mm, v(-50.99, 25.45) * mm, v(-50.94, 25.45) * mm, v(-50.88, 25.45) * mm, v(-50.87, 25.45) * mm, v(-50.54, 25.45) * mm, v(-50.13, 25.45) * mm, v(-49.67, 25.44) * mm, v(-49.65, 25.44) * mm, v(-48.09, 25.43) * mm, v(-46.45, 25.42) * mm, v(-44.8, 25.41) * mm, v(-44.72, 25.41) * mm, v(-38, 25.37) * mm, v(-31.35, 25.34) * mm, v(-25.12, 25.31) * mm, v(-24.8, 25.31) * mm, v(-12.16, 25.27) * mm, v(1.27, 25.26) * mm, v(14.78, 25.28) * mm, v(15.48, 25.29) * mm, v(21.75, 25.3) * mm, v(28.45, 25.32) * mm, v(35.2, 25.36) * mm, v(35.57, 25.36) * mm, v(38.27, 25.37) * mm, v(41.57, 25.4) * mm, v(45.36, 25.41) * mm, v(45.57, 25.42) * mm, v(47.14, 25.43) * mm, v(48.8, 25.44) * mm, v(50.47, 25.45) * mm, v(50.56, 25.45) * mm, v(50.75, 25.45) * mm, v(50.96, 25.45) * mm, v(51.17, 25.45) * mm, v(51.18, 25.45) * mm, v(51.29, 25.45) * mm, v(51.39, 25.45) * mm, v(51.49, 25.43) * mm, v(51.5, 25.43) * mm, v(51.59, 25.42) * mm, v(51.69, 25.4) * mm, v(51.79, 25.37) * mm, v(51.8, 25.37) * mm, v(51.98, 25.3) * mm, v(52.17, 25.22) * mm, v(52.34, 25.1) * mm, v(52.35, 25.1) * mm, v(52.51, 24.99) * mm, v(52.66, 24.85) * mm, v(52.8, 24.68) * mm, v(52.8, 24.67) * mm, v(52.93, 24.52) * mm, v(53.04, 24.34) * mm, v(53.13, 24.15) * mm, v(53.14, 24.14) * mm, v(53.22, 23.96) * mm, v(53.28, 23.76) * mm, v(53.32, 23.55) * mm, v(53.32, 23.54) * mm, v(53.34, 23.44) * mm, v(53.35, 23.33) * mm, v(53.36, 23.23) * mm, v(53.36, 23.22) * mm, v(53.36, 23.18) * mm, v(53.37, 23.13) * mm, v(53.37, 23.07) * mm, v(53.37, 23.07) * mm, v(53.37, 23.06) * mm, v(53.37, 23) * mm, v(53.37, 22.91) * mm, v(53.37, 22.9) * mm, v(53.37, 22.8) * mm, v(53.37, 22.7) * mm, v(53.37, 22.6) * mm, v(53.37, 22.6) * mm, v(53.37, 22.58) * mm, v(53.37, 22.48) * mm, v(53.38, 22.27) * mm, v(53.38, 22.27) * mm], "construction": true});
            skLineSegment(sketch, "E33.bottom", {"start": v(1.74, 25.27) * mm, "end": v(-2, 25.27) * mm});
            skLineSegment(sketch, "E33.top", {"start": v(2, 16) * mm, "end": v(-2, 16) * mm});
            skLineSegment(sketch, "E33.left", {"start": v(2, 28) * mm, "end": v(2, 16) * mm});
            skLineSegment(sketch, "E33.right", {"start": v(-2, 28) * mm, "end": v(-2, 16) * mm});
            skLineSegment(sketch, "E34", {"start": v(0, 0) * mm, "end": v(-8.76, 0) * mm, "construction": true});
            skLineSegment(sketch, "E35.MirrorCS", {"start": v(2, -16) * mm, "end": v(-2, -16) * mm});
            skLineSegment(sketch, "E36.MirrorCS", {"start": v(2, -28) * mm, "end": v(2, -16) * mm});
            skLineSegment(sketch, "E37.MirrorCS", {"start": v(-2, -28) * mm, "end": v(-2, -16) * mm});
            skLineSegment(sketch, "E38.MirrorCS", {"start": v(1.74, -25.27) * mm, "end": v(-2, -25.27) * mm});
            skFitSpline(sketch, "E39.0", {"points": [v(-53.5, 28) * mm, v(-41, 28) * mm, v(-9.38, 28) * mm, v(28.42, 28) * mm, v(53.5, 28) * mm], "construction": true});
            skLineSegment(sketch, "E40", {"start": v(2, 28) * mm, "end": v(-2, 28) * mm});
            skLineSegment(sketch, "E41", {"start": v(2, -28) * mm, "end": v(-2, -28) * mm});
            skSolve(sketch);
        }
        {
            var Q0;
            Q0 = qSketchRegion(id + "F12", true);
            extrude(context, id + "F13", {"entities" : qUnion([Q0]), "operationType" : NewBodyOperationType.ADD, "depth" : 4 * mm});
        }
        {
            var Q0;
            Q0=makeQuery(id+"F13.boolean.opBoolean","INTERSECT",EDGE,{"derivedFrom":[makeQuery(id+"F4.opShell","OFFSET_FACE",FACE,{"disambiguationData":[OSD([sQuery(id+"F0.wireOp",EDGE,"E0.rect.bottom"),sQuery(id+"F0.wireOp",EDGE,"E1.filletArc"),sQuery(id+"F0.wireOp",EDGE,"E3.filletArc"),sQuery(id+"F2.wireOp",EDGE,"E13"),sQuery(id+"F2.wireOp",EDGE,"E19"),sQuery(id+"F2.wireOp",EDGE,"E20")])]}),makeQuery(id+"F13.opExtrude","CAP_FACE",FACE,{"disambiguationData":[OSD([sQuery(id+"F12.wireOp",EDGE,"E33.top"),sQuery(id+"F12.wireOp",EDGE,"E33.left"),sQuery(id+"F12.wireOp",EDGE,"E33.right"),sQuery(id+"F12.wireOp",EDGE,"E40")])],"isStart":false})]});
            var Q1;
            Q1=makeQuery(id+"F13.boolean.opBoolean","INTERSECT",EDGE,{"derivedFrom":[makeQuery(id+"F4.opShell","OFFSET_FACE",FACE,{"disambiguationData":[OSD([sQuery(id+"F0.wireOp",EDGE,"E0.rect.bottom"),sQuery(id+"F0.wireOp",EDGE,"E1.filletArc"),sQuery(id+"F0.wireOp",EDGE,"E3.filletArc"),sQuery(id+"F2.wireOp",EDGE,"E13"),sQuery(id+"F2.wireOp",EDGE,"E19"),sQuery(id+"F2.wireOp",EDGE,"E20")])]}),makeQuery(id+"F13.opExtrude","CAP_FACE",FACE,{"disambiguationData":[OSD([sQuery(id+"F12.wireOp",EDGE,"E35.MirrorCS"),sQuery(id+"F12.wireOp",EDGE,"E36.MirrorCS"),sQuery(id+"F12.wireOp",EDGE,"E37.MirrorCS"),sQuery(id+"F12.wireOp",EDGE,"E41")])],"isStart":false})]});
            chamfer(context, id + "F14", {"entities" : qUnion([Q0, Q1]), "width" : 10 * mm, "tangentPropagation" : true});
        }
    });
